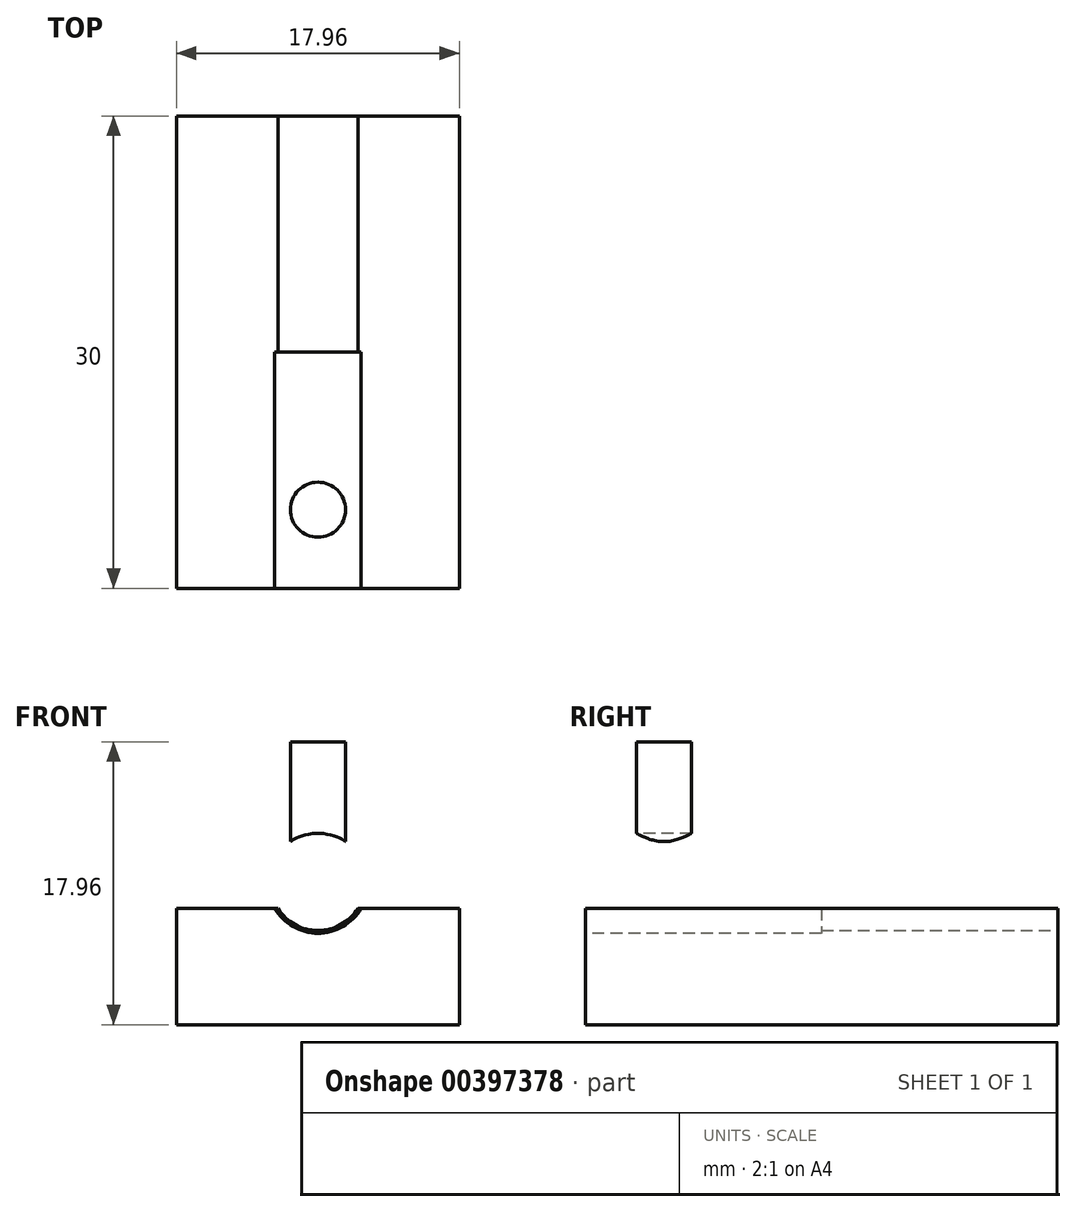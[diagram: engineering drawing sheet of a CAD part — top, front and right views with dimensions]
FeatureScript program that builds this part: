
annotation { "Feature Type Name" : "Feature", "Feature Type Description" : "" }
export const myFeature = defineFeature(function(context is Context, id is Id, definition is map)
    precondition{}
    {
        {
            var Q0;
            Q0=qCreatedBy(makeId("Front.planeOp"),FACE);
            var sketch = newSketch(context, id + "F0", { "sketchPlane" : qUnion([Q0])});
            skLineSegment(sketch, "E0.bottom", {"start": v(0, 0) * mm, "end": v(17.96, 0) * mm});
            skLineSegment(sketch, "E0.top", {"start": v(0, 17.96) * mm, "end": v(17.96, 17.96) * mm});
            skLineSegment(sketch, "E0.left", {"start": v(0, 0) * mm, "end": v(0, 17.96) * mm});
            skLineSegment(sketch, "E0.right", {"start": v(17.96, 0) * mm, "end": v(17.96, 17.96) * mm});
            skSolve(sketch);
        }
        {
            var Q0;
            Q0 = qSketchRegion(id + "F0", true);
            extrude(context, id + "F1", {"entities" : qUnion([Q0]), "depth" : 30 * mm});
        }
        {
            var Q0;
            Q0=makeQuery(id+"F1.opExtrude","CAP_FACE",FACE,{"disambiguationData":[OSD([sQuery(id+"F0.wireOp",EDGE,"E0.bottom"),sQuery(id+"F0.wireOp",EDGE,"E0.top"),sQuery(id+"F0.wireOp",EDGE,"E0.left"),sQuery(id+"F0.wireOp",EDGE,"E0.right")])],"isStart":false});
            var sketch = newSketch(context, id + "F2", { "sketchPlane" : qUnion([Q0])});
            skCircle(sketch, "E1", {"center": v(8.98, 8.98) * mm, "radius": 3.18 * mm});
            skPoint(sketch, "E1.centerSnap0", {"position": v(8.98, 17.96) * mm});
            skPoint(sketch, "E1.centerSnap1", {"position": v(0, 8.98) * mm});
            skSolve(sketch);
        }
        {
            var Q0;
            Q0=makeQuery(id+"F2.imprint","IMPRINT",FACE,{"disambiguationData":[TD([[makeQuery(id+"F2.imprint","IMPRINT",EDGE,{"derivedFrom":sQuery(id+"F2.wireOp",EDGE,"E1")}),1.0]])]});
            extrude(context, id + "F3", {"entities" : qUnion([Q0]), "operationType" : NewBodyOperationType.REMOVE, "oppositeDirection" : true, "depth" : 15 * mm});
        }
        {
            var Q0;
            Q0=makeQuery(id+"F1.opExtrude","CAP_FACE",FACE,{"disambiguationData":[OSD([sQuery(id+"F0.wireOp",EDGE,"E0.bottom"),sQuery(id+"F0.wireOp",EDGE,"E0.top"),sQuery(id+"F0.wireOp",EDGE,"E0.left"),sQuery(id+"F0.wireOp",EDGE,"E0.right")])],"isStart":true});
            var sketch = newSketch(context, id + "F4", { "sketchPlane" : qUnion([Q0])});
            skCircle(sketch, "E2", {"center": v(-8.98, 8.98) * mm, "radius": 3 * mm});
            skPoint(sketch, "E2.centerSnap0", {"position": v(-8.98, 17.96) * mm});
            skPoint(sketch, "E2.centerSnap1", {"position": v(0, 8.98) * mm});
            skSolve(sketch);
        }
        {
            var Q0;
            Q0=makeQuery(id+"F4.imprint","IMPRINT",FACE,{"disambiguationData":[TD([[makeQuery(id+"F4.imprint","IMPRINT",EDGE,{"derivedFrom":sQuery(id+"F4.wireOp",EDGE,"E2")}),1.0]])]});
            extrude(context, id + "F5", {"entities" : qUnion([Q0]), "operationType" : NewBodyOperationType.REMOVE, "oppositeDirection" : true, "depth" : 15 * mm});
        }
        {
            var Q0;
            Q0=makeQuery(id+"F1.opExtrude","SWEPT_FACE",FACE,{"disambiguationData":[OSD([sQuery(id+"F0.wireOp",EDGE,"E0.top")])]});
            var sketch = newSketch(context, id + "F6", { "sketchPlane" : qUnion([Q0])});
            skLineSegment(sketch, "E3", {"start": v(8.98, -30) * mm, "end": v(8.98, 0) * mm});
            skPoint(sketch, "E4", {"position": v(8.98, -15) * mm});
            skPoint(sketch, "E5", {"position": v(8.98, -25) * mm});
            skPoint(sketch, "E6", {"position": v(8.98, -5) * mm});
            skCircle(sketch, "E7", {"center": v(8.98, -25) * mm, "radius": 1.75 * mm});
            skCircle(sketch, "E8", {"center": v(8.98, -5) * mm, "radius": 1.75 * mm});
            skSolve(sketch);
        }
        {
            var Q0;
            {var subQ0=sQuery(id+"F6.wireOp",EDGE,"E7");var subQ1=sQuery(id+"F6.wireOp",EDGE,"E3");var subQ2=makeQuery(id+"F6.imprint","INTERSECT",VERTEX,{"disambiguationData":[OD(0.0)],"derivedFrom":[subQ1,subQ0]});Q0=makeQuery(id+"F6.imprint","IMPRINT",FACE,{"disambiguationData":[TD([[makeQuery(id+"F6.imprint","IMPRINT",EDGE,{"disambiguationData":[TD([[subQ2,-1.0]])],"derivedFrom":subQ1}),1.0]])]});}
            var Q1;
            {var subQ0=sQuery(id+"F6.wireOp",EDGE,"E7");var subQ1=sQuery(id+"F6.wireOp",EDGE,"E3");var subQ2=makeQuery(id+"F6.imprint","INTERSECT",VERTEX,{"disambiguationData":[OD(0.0)],"derivedFrom":[subQ1,subQ0]});Q1=makeQuery(id+"F6.imprint","IMPRINT",FACE,{"disambiguationData":[TD([[makeQuery(id+"F6.imprint","IMPRINT",EDGE,{"disambiguationData":[TD([[subQ2,-1.0]])],"derivedFrom":subQ1}),-1.0]])]});}
            var Q2;
            {var subQ0=sQuery(id+"F6.wireOp",EDGE,"E8");var subQ1=sQuery(id+"F6.wireOp",EDGE,"E3");var subQ2=makeQuery(id+"F6.imprint","INTERSECT",VERTEX,{"disambiguationData":[OD(0.0)],"derivedFrom":[subQ1,subQ0]});Q2=makeQuery(id+"F6.imprint","IMPRINT",FACE,{"disambiguationData":[TD([[makeQuery(id+"F6.imprint","IMPRINT",EDGE,{"disambiguationData":[TD([[subQ2,-1.0]])],"derivedFrom":subQ1}),1.0]])]});}
            var Q3;
            {var subQ0=sQuery(id+"F6.wireOp",EDGE,"E8");var subQ1=sQuery(id+"F6.wireOp",EDGE,"E3");var subQ2=makeQuery(id+"F6.imprint","INTERSECT",VERTEX,{"disambiguationData":[OD(0.0)],"derivedFrom":[subQ1,subQ0]});Q3=makeQuery(id+"F6.imprint","IMPRINT",FACE,{"disambiguationData":[TD([[makeQuery(id+"F6.imprint","IMPRINT",EDGE,{"disambiguationData":[TD([[subQ2,-1.0]])],"derivedFrom":subQ1}),-1.0]])]});}
            extrude(context, id + "F7", {"entities" : qUnion([Q0, Q1, Q2, Q3]), "operationType" : NewBodyOperationType.REMOVE, "oppositeDirection" : true, "depth" : 10.58 * mm});
        }
        {
            var Q0;
            Q0=makeQuery(id+"F1.opExtrude","SWEPT_FACE",FACE,{"disambiguationData":[OSD([sQuery(id+"F0.wireOp",EDGE,"E0.right")])]});
            var sketch = newSketch(context, id + "F8", { "sketchPlane" : qUnion([Q0])});
            skLineSegment(sketch, "E9", {"start": v(-30, 8.98) * mm, "end": v(0, 8.98) * mm});
            skPoint(sketch, "E10", {"position": v(-20, 8.98) * mm});
            skPoint(sketch, "E11", {"position": v(-15, 8.98) * mm});
            skPoint(sketch, "E12", {"position": v(-10, 8.98) * mm});
            skCircle(sketch, "E13", {"center": v(-20, 8.98) * mm, "radius": 3.18 * mm});
            skCircle(sketch, "E14", {"center": v(-10, 8.98) * mm, "radius": 3.17 * mm});
            skLineSegment(sketch, "E15", {"start": v(-22.06, 11.4) * mm, "end": v(-17.94, 11.4) * mm});
            skLineSegment(sketch, "E16", {"start": v(-12.06, 11.4) * mm, "end": v(-7.94, 11.4) * mm});
            skLineSegment(sketch, "E17", {"start": v(-30, 13.14) * mm, "end": v(0, 13.14) * mm});
            skCircle(sketch, "E18", {"center": v(-20, 13.14) * mm, "radius": 1.75 * mm});
            skCircle(sketch, "E19", {"center": v(-10, 13.14) * mm, "radius": 1.75 * mm});
            skSolve(sketch);
        }
        {
            var Q0;
            {var subQ0=sQuery(id+"F8.wireOp",EDGE,"E18");var subQ1=sQuery(id+"F8.wireOp",EDGE,"E13");var subQ2=makeQuery(id+"F8.imprint","INTERSECT",VERTEX,{"disambiguationData":[OD(0.0)],"derivedFrom":[subQ1,subQ0]});Q0=makeQuery(id+"F8.imprint","IMPRINT",FACE,{"disambiguationData":[TD([[makeQuery(id+"F8.imprint","IMPRINT",EDGE,{"disambiguationData":[TD([[subQ2,-1.0]])],"derivedFrom":subQ1}),-1.0]])]});}
            var Q1;
            {var subQ0=sQuery(id+"F8.wireOp",EDGE,"E18");var subQ1=sQuery(id+"F8.wireOp",EDGE,"E13");var subQ2=makeQuery(id+"F8.imprint","INTERSECT",VERTEX,{"disambiguationData":[OD(0.0)],"derivedFrom":[subQ1,subQ0]});Q1=makeQuery(id+"F8.imprint","IMPRINT",FACE,{"disambiguationData":[TD([[makeQuery(id+"F8.imprint","IMPRINT",EDGE,{"disambiguationData":[TD([[subQ2,-1.0]])],"derivedFrom":subQ1}),1.0]])]});}
            var Q2;
            {var subQ0=sQuery(id+"F8.wireOp",EDGE,"E18");var subQ1=sQuery(id+"F8.wireOp",EDGE,"E17");var subQ2=makeQuery(id+"F8.imprint","INTERSECT",VERTEX,{"disambiguationData":[OD(0.0)],"derivedFrom":[subQ1,subQ0]});Q2=makeQuery(id+"F8.imprint","IMPRINT",FACE,{"disambiguationData":[TD([[makeQuery(id+"F8.imprint","IMPRINT",EDGE,{"disambiguationData":[TD([[subQ2,-1.0]])],"derivedFrom":subQ1}),1.0]])]});}
            var Q3;
            {var subQ0=sQuery(id+"F8.wireOp",EDGE,"E19");var subQ1=sQuery(id+"F8.wireOp",EDGE,"E14");var subQ2=makeQuery(id+"F8.imprint","INTERSECT",VERTEX,{"disambiguationData":[OD(0.0)],"derivedFrom":[subQ1,subQ0]});Q3=makeQuery(id+"F8.imprint","IMPRINT",FACE,{"disambiguationData":[TD([[makeQuery(id+"F8.imprint","IMPRINT",EDGE,{"disambiguationData":[TD([[subQ2,-1.0]])],"derivedFrom":subQ1}),1.0]])]});}
            var Q4;
            {var subQ0=sQuery(id+"F8.wireOp",EDGE,"E19");var subQ1=sQuery(id+"F8.wireOp",EDGE,"E14");var subQ2=makeQuery(id+"F8.imprint","INTERSECT",VERTEX,{"disambiguationData":[OD(0.0)],"derivedFrom":[subQ1,subQ0]});Q4=makeQuery(id+"F8.imprint","IMPRINT",FACE,{"disambiguationData":[TD([[makeQuery(id+"F8.imprint","IMPRINT",EDGE,{"disambiguationData":[TD([[subQ2,-1.0]])],"derivedFrom":subQ1}),-1.0]])]});}
            var Q5;
            {var subQ0=sQuery(id+"F8.wireOp",EDGE,"E19");var subQ1=sQuery(id+"F8.wireOp",EDGE,"E17");var subQ2=makeQuery(id+"F8.imprint","INTERSECT",VERTEX,{"disambiguationData":[OD(0.0)],"derivedFrom":[subQ1,subQ0]});Q5=makeQuery(id+"F8.imprint","IMPRINT",FACE,{"disambiguationData":[TD([[makeQuery(id+"F8.imprint","IMPRINT",EDGE,{"disambiguationData":[TD([[subQ2,-1.0]])],"derivedFrom":subQ1}),1.0]])]});}
            extrude(context, id + "F9", {"entities" : qUnion([Q0, Q1, Q2, Q3, Q4, Q5]), "operationType" : NewBodyOperationType.REMOVE, "oppositeDirection" : true, "depth" : 51.32 * mm});
        }
    });
